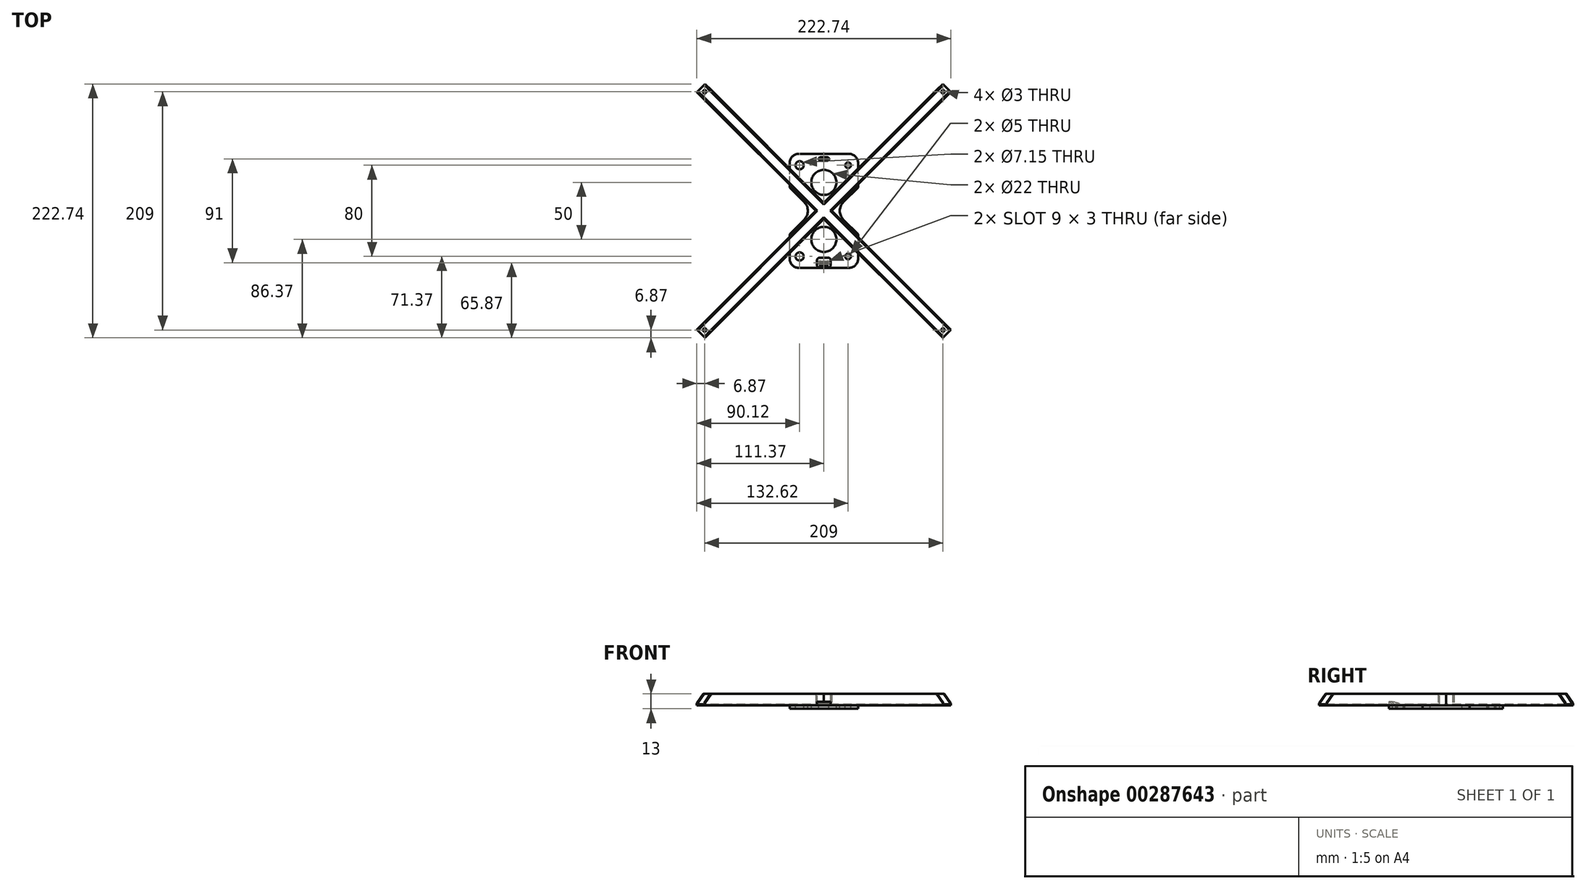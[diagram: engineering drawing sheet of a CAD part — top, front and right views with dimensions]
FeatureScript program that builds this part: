
annotation { "Feature Type Name" : "Feature", "Feature Type Description" : "" }
export const myFeature = defineFeature(function(context is Context, id is Id, definition is map)
    precondition{}
    {
        {
            var Q0;
            Q0=qCreatedBy(makeId("Top.planeOp"),FACE);
            var sketch = newSketch(context, id + "F0", { "sketchPlane" : qUnion([Q0])});
            skLineSegment(sketch, "E0.bottom", {"start": v(30, -50) * mm, "end": v(-30, -50) * mm});
            skLineSegment(sketch, "E0.top", {"start": v(30, 50) * mm, "end": v(-30, 50) * mm});
            skLineSegment(sketch, "E0.left", {"start": v(30, -50) * mm, "end": v(30, 50) * mm});
            skLineSegment(sketch, "E0.right", {"start": v(-30, -50) * mm, "end": v(-30, 50) * mm});
            skPoint(sketch, "E0.middle", {"position": v(0, 0) * mm});
            skSolve(sketch);
        }
        {
            var Q0;
            Q0 = qSketchRegion(id + "F0", true);
            extrude(context, id + "F1", {"entities" : qUnion([Q0]), "depth" : 3 * mm, "offsetDistance" : 25 * mm});
        }
        {
            var Q0;
            Q0=makeQuery(id+"F1.opExtrude","CAP_FACE",FACE,{"disambiguationData":[OSD([sQuery(id+"F0.wireOp",EDGE,"E0.bottom"),sQuery(id+"F0.wireOp",EDGE,"E0.top"),sQuery(id+"F0.wireOp",EDGE,"E0.left"),sQuery(id+"F0.wireOp",EDGE,"E0.right")])],"isStart":false});
            var sketch = newSketch(context, id + "F2", { "sketchPlane" : qUnion([Q0])});
            skCircle(sketch, "E1", {"center": v(0, 25) * mm, "radius": 11 * mm});
            skCircle(sketch, "E2", {"center": v(0, -25) * mm, "radius": 11 * mm});
            skCircle(sketch, "E3", {"center": v(25, 0) * mm, "radius": 11 * mm});
            skCircle(sketch, "E4", {"center": v(-25, 0) * mm, "radius": 11 * mm});
            skLineSegment(sketch, "E5", {"start": v(-3, 45.5) * mm, "end": v(3, 45.5) * mm});
            skLineSegment(sketch, "E6", {"start": v(-3, -45.5) * mm, "end": v(3, -45.5) * mm});
            skPoint(sketch, "E7", {"position": v(0, 45.5) * mm});
            skArc(sketch, "E8.0.startCap", {"start": v(-3, 44) * mm, "mid": v(-4.5, 45.5) * mm, "end": v(-3, 47) * mm});
            skArc(sketch, "E8.0.endCap", {"start": v(3, 47) * mm, "mid": v(4.5, 45.5) * mm, "end": v(3, 44) * mm});
            skLineSegment(sketch, "E8.0.left", {"start": v(-3, 47) * mm, "end": v(3, 47) * mm});
            skLineSegment(sketch, "E8.0.right", {"start": v(-3, 44) * mm, "end": v(3, 44) * mm});
            skArc(sketch, "E9.0.startCap", {"start": v(-3, -47) * mm, "mid": v(-4.5, -45.5) * mm, "end": v(-3, -44) * mm});
            skArc(sketch, "E9.0.endCap", {"start": v(3, -44) * mm, "mid": v(4.5, -45.5) * mm, "end": v(3, -47) * mm});
            skLineSegment(sketch, "E9.0.left", {"start": v(-3, -44) * mm, "end": v(3, -44) * mm});
            skLineSegment(sketch, "E9.0.right", {"start": v(-3, -47) * mm, "end": v(3, -47) * mm});
            skSolve(sketch);
        }
        {
            var Q0;
            Q0=makeQuery(id+"F2.imprint","IMPRINT",FACE,{"disambiguationData":[TD([[makeQuery(id+"F2.imprint","IMPRINT",EDGE,{"derivedFrom":sQuery(id+"F2.wireOp",EDGE,"E1")}),-1.0]])]});
            var sketch = newSketch(context, id + "F3", { "sketchPlane" : qUnion([Q0])});
            skLineSegment(sketch, "E10.bottom", {"start": v(21.25, 40) * mm, "end": v(-21.25, 40) * mm, "construction": true});
            skLineSegment(sketch, "E10.top", {"start": v(21.25, -40) * mm, "end": v(-21.25, -40) * mm, "construction": true});
            skLineSegment(sketch, "E10.left", {"start": v(21.25, 40) * mm, "end": v(21.25, -40) * mm, "construction": true});
            skLineSegment(sketch, "E10.right", {"start": v(-21.25, 40) * mm, "end": v(-21.25, -40) * mm, "construction": true});
            skPoint(sketch, "E10.middle", {"position": v(0, 0) * mm});
            skCircle(sketch, "E11", {"center": v(21.25, 40) * mm, "radius": 2.5 * mm});
            skCircle(sketch, "E12", {"center": v(21.25, -40) * mm, "radius": 2.5 * mm});
            skCircle(sketch, "E13", {"center": v(-21.25, -40) * mm, "radius": 3.58 * mm});
            skCircle(sketch, "E14", {"center": v(-21.25, 40) * mm, "radius": 3.57 * mm});
            skSolve(sketch);
        }
        {
            var Q0;
            Q0 = qSketchRegion(id + "F3", true);
            extrude(context, id + "F4", {"entities" : qUnion([Q0]), "operationType" : NewBodyOperationType.REMOVE, "endBound" : BoundingType.THROUGH_ALL, "oppositeDirection" : true, "depth" : 25 * mm, "offsetDistance" : 25 * mm});
        }
        {
            var Q0;
            Q0 = qSketchRegion(id + "F2", true);
            extrude(context, id + "F5", {"entities" : qUnion([Q0]), "operationType" : NewBodyOperationType.REMOVE, "endBound" : BoundingType.THROUGH_ALL, "oppositeDirection" : true, "depth" : 25 * mm, "offsetDistance" : 25 * mm});
        }
        {
            var Q0;
            Q0=makeQuery(id+"F1.opExtrude","CAP_FACE",FACE,{"disambiguationData":[OSD([sQuery(id+"F0.wireOp",EDGE,"E0.bottom"),sQuery(id+"F0.wireOp",EDGE,"E0.top"),sQuery(id+"F0.wireOp",EDGE,"E0.left"),sQuery(id+"F0.wireOp",EDGE,"E0.right")])],"isStart":false});
            var sketch = newSketch(context, id + "F6", { "sketchPlane" : qUnion([Q0])});
            skLineSegment(sketch, "E15", {"start": v(30, 20.56) * mm, "end": v(30, -20.56) * mm});
            skLineSegment(sketch, "E16", {"start": v(30, -20.56) * mm, "end": v(17.22, -7.78) * mm});
            skLineSegment(sketch, "E17", {"start": v(17.22, -7.78) * mm, "end": v(17.22, 7.78) * mm});
            skLineSegment(sketch, "E18", {"start": v(17.22, 7.78) * mm, "end": v(30, 20.56) * mm});
            skLineSegment(sketch, "E19", {"start": v(-30, 20.56) * mm, "end": v(-17.22, 7.78) * mm});
            skLineSegment(sketch, "E20", {"start": v(-17.22, 7.78) * mm, "end": v(-17.22, -7.78) * mm});
            skLineSegment(sketch, "E21", {"start": v(-17.22, -7.78) * mm, "end": v(-30, -20.56) * mm});
            skLineSegment(sketch, "E22", {"start": v(-30, -20.56) * mm, "end": v(-30, 20.56) * mm});
            skSolve(sketch);
        }
        {
            var Q0;
            Q0 = qSketchRegion(id + "F6", true);
            extrude(context, id + "F7", {"entities" : qUnion([Q0]), "operationType" : NewBodyOperationType.REMOVE, "endBound" : BoundingType.THROUGH_ALL, "oppositeDirection" : true, "depth" : 25 * mm, "offsetDistance" : 25 * mm});
        }
        {
            var Q0;
            Q0=makeQuery(id+"F1.opExtrude","SWEPT_EDGE",EDGE,{"disambiguationData":[OSD([sQuery(id+"F0.wireOp",EDGE,"E0.bottom"),sQuery(id+"F0.wireOp",EDGE,"E0.left")])]});
            var Q1;
            Q1=makeQuery(id+"F1.opExtrude","SWEPT_EDGE",EDGE,{"disambiguationData":[OSD([sQuery(id+"F0.wireOp",EDGE,"E0.bottom"),sQuery(id+"F0.wireOp",EDGE,"E0.right")])]});
            var Q2;
            Q2=makeQuery(id+"F1.opExtrude","SWEPT_EDGE",EDGE,{"disambiguationData":[OSD([sQuery(id+"F0.wireOp",EDGE,"E0.top"),sQuery(id+"F0.wireOp",EDGE,"E0.left")])]});
            var Q3;
            Q3=makeQuery(id+"F1.opExtrude","SWEPT_EDGE",EDGE,{"disambiguationData":[OSD([sQuery(id+"F0.wireOp",EDGE,"E0.top"),sQuery(id+"F0.wireOp",EDGE,"E0.right")])]});
            fillet(context, id + "F8", {"entities" : qUnion([Q0, Q1, Q2, Q3]), "radius" : 8 * mm, "tangentPropagation" : true, "allowEdgeOverflow" : false});
        }
        {
            var Q0;
            Q0=makeQuery(id+"F1.opExtrude","CAP_FACE",FACE,{"disambiguationData":[OSD([sQuery(id+"F0.wireOp",EDGE,"E0.bottom"),sQuery(id+"F0.wireOp",EDGE,"E0.top"),sQuery(id+"F0.wireOp",EDGE,"E0.left"),sQuery(id+"F0.wireOp",EDGE,"E0.right")])],"isStart":false});
            var sketch = newSketch(context, id + "F9", { "sketchPlane" : qUnion([Q0])});
            skLineSegment(sketch, "E23", {"start": v(-107.83, 107.83) * mm, "end": v(107.83, -107.83) * mm, "construction": true});
            skLineSegment(sketch, "E24", {"start": v(-104.3, 111.37) * mm, "end": v(-111.37, 104.3) * mm});
            skLineSegment(sketch, "E25", {"start": v(-111.37, 104.3) * mm, "end": v(104.3, -111.37) * mm});
            skLineSegment(sketch, "E26", {"start": v(104.3, -111.37) * mm, "end": v(111.37, -104.3) * mm});
            skLineSegment(sketch, "E27", {"start": v(111.37, -104.3) * mm, "end": v(-104.3, 111.37) * mm});
            skSolve(sketch);
        }
        {
            var Q0;
            Q0 = qSketchRegion(id + "F9", true);
            extrude(context, id + "F10", {"entities" : qUnion([Q0]), "depth" : 10 * mm, "offsetDistance" : 25 * mm});
        }
        {
            var Q0;
            Q0=makeQuery(id+"F10.opExtrude","CAP_FACE",FACE,{"disambiguationData":[OSD([sQuery(id+"F9.wireOp",EDGE,"E24"),sQuery(id+"F9.wireOp",EDGE,"E25"),sQuery(id+"F9.wireOp",EDGE,"E26"),sQuery(id+"F9.wireOp",EDGE,"E27")])],"isStart":false});
            var sketch = newSketch(context, id + "F11", { "sketchPlane" : qUnion([Q0])});
            skLineSegment(sketch, "E28", {"start": v(-105, 110.66) * mm, "end": v(-110.66, 105) * mm});
            skLineSegment(sketch, "E29", {"start": v(-110.66, 105) * mm, "end": v(105, -110.66) * mm});
            skLineSegment(sketch, "E30", {"start": v(105, -110.66) * mm, "end": v(110.66, -105) * mm});
            skLineSegment(sketch, "E31", {"start": v(110.66, -105) * mm, "end": v(-105, 110.66) * mm});
            skSolve(sketch);
        }
        {
            var Q0;
            Q0 = qSketchRegion(id + "F11", true);
            extrude(context, id + "F12", {"entities" : qUnion([Q0]), "operationType" : NewBodyOperationType.REMOVE, "oppositeDirection" : true, "depth" : 9 * mm, "offsetDistance" : 25 * mm});
        }
        {
            var Q0;
            Q0=makeQuery(id+"F10.opExtrude","SWEPT_FACE",FACE,{"disambiguationData":[OSD([sQuery(id+"F9.wireOp",EDGE,"E27")])]});
            var sketch = newSketch(context, id + "F13", { "sketchPlane" : qUnion([Q0])});
            skLineSegment(sketch, "E32.bottom", {"start": v(5, 13) * mm, "end": v(-5, 13) * mm});
            skLineSegment(sketch, "E32.top", {"start": v(5, 3) * mm, "end": v(-5, 3) * mm});
            skLineSegment(sketch, "E32.left", {"start": v(5, 13) * mm, "end": v(5, 3) * mm});
            skLineSegment(sketch, "E32.right", {"start": v(-5, 13) * mm, "end": v(-5, 3) * mm});
            skSolve(sketch);
        }
        {
            var Q0;
            Q0 = qSketchRegion(id + "F13", true);
            extrude(context, id + "F14", {"entities" : qUnion([Q0]), "depth" : (305 / 2 - 5) * mm, "offsetDistance" : 25 * mm});
        }
        {
            var Q0;
            Q0=makeQuery(id+"F14.opExtrude","CAP_FACE",FACE,{"disambiguationData":[OSD([sQuery(id+"F13.wireOp",EDGE,"E32.bottom"),sQuery(id+"F13.wireOp",EDGE,"E32.top"),sQuery(id+"F13.wireOp",EDGE,"E32.left"),sQuery(id+"F13.wireOp",EDGE,"E32.right")])],"isStart":false});
            var sketch = newSketch(context, id + "F15", { "sketchPlane" : qUnion([Q0])});
            skLineSegment(sketch, "E33.bottom", {"start": v(4, 13) * mm, "end": v(-4, 13) * mm});
            skLineSegment(sketch, "E33.top", {"start": v(4, 4) * mm, "end": v(-4, 4) * mm});
            skLineSegment(sketch, "E33.left", {"start": v(4, 13) * mm, "end": v(4, 4) * mm});
            skLineSegment(sketch, "E33.right", {"start": v(-4, 13) * mm, "end": v(-4, 4) * mm});
            skSolve(sketch);
        }
        {
            var Q0;
            Q0 = qSketchRegion(id + "F15", true);
            extrude(context, id + "F16", {"entities" : qUnion([Q0]), "operationType" : NewBodyOperationType.REMOVE, "endBound" : BoundingType.THROUGH_ALL, "oppositeDirection" : true, "depth" : 25 * mm, "offsetDistance" : 25 * mm});
        }
        {
            var Q0;
            Q0=qCreatedBy(makeId("Front.planeOp"),FACE);
            var Q1;
            Q1=qCreatedBy(makeId("Right.planeOp"),FACE);
            cPlane(context, id + "F17", {"entities" : qUnion([Q0, Q1]), "cplaneType" : CPlaneType.MID_PLANE, "offset" : 25 * mm, "width" : 150 * mm, "height" : 150 * mm});
        }
        {
            var Q0;
            Q0=makeQuery(id+"F14.opExtrude","SWEPT_BODY",BODY,{"disambiguationData":[OSD([sQuery(id+"F13.wireOp",EDGE,"E32.bottom"),sQuery(id+"F13.wireOp",EDGE,"E32.top"),sQuery(id+"F13.wireOp",EDGE,"E32.left"),sQuery(id+"F13.wireOp",EDGE,"E32.right")])]});
            var Q1;
            Q1=qCreatedBy(id+"F17.planeOp",FACE);
            mirror(context, id + "F18", {"entities" : qUnion([Q0]), "mirrorPlane" : qUnion([Q1])});
        }
        {
            var Q0;
            {var subQ0=sQuery(id+"F13.wireOp",EDGE,"E32.bottom");var subQ1=sQuery(id+"F13.wireOp",EDGE,"E32.left");Q0=makeQuery(id+"F16.boolean.opBoolean","SPLIT",EDGE,{"disambiguationData":[TD([makeQuery(id+"F14.opExtrude","SWEPT_FACE",FACE,{"disambiguationData":[OSD([subQ1])]})])],"derivedFrom":makeQuery(id+"F14.opExtrude","CAP_EDGE",EDGE,{"disambiguationData":[OSD([subQ0])],"isStart":false})});}
            var Q1;
            {var subQ0=sQuery(id+"F13.wireOp",EDGE,"E32.bottom");var subQ1=sQuery(id+"F13.wireOp",EDGE,"E32.right");Q1=makeQuery(id+"F16.boolean.opBoolean","SPLIT",EDGE,{"disambiguationData":[TD([makeQuery(id+"F14.opExtrude","SWEPT_FACE",FACE,{"disambiguationData":[OSD([subQ1])]})])],"derivedFrom":makeQuery(id+"F14.opExtrude","CAP_EDGE",EDGE,{"disambiguationData":[OSD([subQ0])],"isStart":false})});}
            var Q2;
            {var subQ0=sQuery(id+"F9.wireOp",EDGE,"E26");var subQ1=sQuery(id+"F9.wireOp",EDGE,"E25");Q2=makeQuery(id+"F12.boolean.opBoolean","SPLIT",EDGE,{"disambiguationData":[TD([makeQuery(id+"F10.opExtrude","SWEPT_FACE",FACE,{"disambiguationData":[OSD([subQ1])]})])],"derivedFrom":makeQuery(id+"F10.opExtrude","CAP_EDGE",EDGE,{"disambiguationData":[OSD([subQ0])],"isStart":false})});}
            var Q3;
            {var subQ0=sQuery(id+"F9.wireOp",EDGE,"E27");var subQ1=sQuery(id+"F9.wireOp",EDGE,"E26");Q3=makeQuery(id+"F12.boolean.opBoolean","SPLIT",EDGE,{"disambiguationData":[TD([makeQuery(id+"F10.opExtrude","SWEPT_FACE",FACE,{"disambiguationData":[OSD([subQ0])]})])],"derivedFrom":makeQuery(id+"F10.opExtrude","CAP_EDGE",EDGE,{"disambiguationData":[OSD([subQ1])],"isStart":false})});}
            var Q4;
            {var subQ0=sQuery(id+"F13.wireOp",EDGE,"E32.bottom");var subQ1=sQuery(id+"F13.wireOp",EDGE,"E32.right");Q4=makeQuery(id+"F18.opPattern","COPY",EDGE,{"derivedFrom":makeQuery(id+"F16.boolean.opBoolean","SPLIT",EDGE,{"disambiguationData":[TD([makeQuery(id+"F14.opExtrude","SWEPT_FACE",FACE,{"disambiguationData":[OSD([subQ1])]})])],"derivedFrom":makeQuery(id+"F14.opExtrude","CAP_EDGE",EDGE,{"disambiguationData":[OSD([subQ0])],"isStart":false})}),"instanceName":"1"});}
            var Q5;
            {var subQ0=sQuery(id+"F13.wireOp",EDGE,"E32.bottom");var subQ1=sQuery(id+"F13.wireOp",EDGE,"E32.left");Q5=makeQuery(id+"F18.opPattern","COPY",EDGE,{"derivedFrom":makeQuery(id+"F16.boolean.opBoolean","SPLIT",EDGE,{"disambiguationData":[TD([makeQuery(id+"F14.opExtrude","SWEPT_FACE",FACE,{"disambiguationData":[OSD([subQ1])]})])],"derivedFrom":makeQuery(id+"F14.opExtrude","CAP_EDGE",EDGE,{"disambiguationData":[OSD([subQ0])],"isStart":false})}),"instanceName":"1"});}
            var Q6;
            {var subQ0=sQuery(id+"F9.wireOp",EDGE,"E24");var subQ1=sQuery(id+"F9.wireOp",EDGE,"E27");Q6=makeQuery(id+"F12.boolean.opBoolean","SPLIT",EDGE,{"disambiguationData":[TD([makeQuery(id+"F10.opExtrude","SWEPT_FACE",FACE,{"disambiguationData":[OSD([subQ1])]})])],"derivedFrom":makeQuery(id+"F10.opExtrude","CAP_EDGE",EDGE,{"disambiguationData":[OSD([subQ0])],"isStart":false})});}
            var Q7;
            {var subQ0=sQuery(id+"F9.wireOp",EDGE,"E24");var subQ1=sQuery(id+"F9.wireOp",EDGE,"E25");Q7=makeQuery(id+"F12.boolean.opBoolean","SPLIT",EDGE,{"disambiguationData":[TD([makeQuery(id+"F10.opExtrude","SWEPT_FACE",FACE,{"disambiguationData":[OSD([subQ1])]})])],"derivedFrom":makeQuery(id+"F10.opExtrude","CAP_EDGE",EDGE,{"disambiguationData":[OSD([subQ0])],"isStart":false})});}
            chamfer(context, id + "F19", {"entities" : qUnion([Q0, Q1, Q2, Q3, Q4, Q5, Q6, Q7]), "width" : 8 * mm, "tangentPropagation" : true});
        }
        {
            var Q0;
            Q0=makeQuery(id+"F12.boolean.opBoolean","COPY",FACE,{"derivedFrom":makeQuery(id+"F12.opExtrude","CAP_FACE",FACE,{"disambiguationData":[OSD([sQuery(id+"F11.wireOp",EDGE,"E28"),sQuery(id+"F11.wireOp",EDGE,"E29"),sQuery(id+"F11.wireOp",EDGE,"E30"),sQuery(id+"F11.wireOp",EDGE,"E31")])],"isStart":false})});
            var sketch = newSketch(context, id + "F20", { "sketchPlane" : qUnion([Q0])});
            skLineSegment(sketch, "E34.bottom", {"start": v(-104.5, -104.5) * mm, "end": v(104.5, -104.5) * mm, "construction": true});
            skLineSegment(sketch, "E34.top", {"start": v(-104.5, 104.5) * mm, "end": v(104.5, 104.5) * mm, "construction": true});
            skLineSegment(sketch, "E34.left", {"start": v(-104.5, -104.5) * mm, "end": v(-104.5, 104.5) * mm, "construction": true});
            skLineSegment(sketch, "E34.right", {"start": v(104.5, -104.5) * mm, "end": v(104.5, 104.5) * mm, "construction": true});
            skPoint(sketch, "E34.middle", {"position": v(0, 0) * mm});
            skCircle(sketch, "E35", {"center": v(-104.5, -104.5) * mm, "radius": 1.5 * mm});
            skCircle(sketch, "E36", {"center": v(104.5, -104.5) * mm, "radius": 1.5 * mm});
            skCircle(sketch, "E37", {"center": v(104.5, 104.5) * mm, "radius": 1.5 * mm});
            skCircle(sketch, "E38", {"center": v(-104.5, 104.5) * mm, "radius": 1.5 * mm});
            skSolve(sketch);
        }
        {
            var Q0;
            Q0 = qSketchRegion(id + "F20", true);
            extrude(context, id + "F21", {"entities" : qUnion([Q0]), "operationType" : NewBodyOperationType.REMOVE, "endBound" : BoundingType.THROUGH_ALL, "oppositeDirection" : true, "depth" : 25 * mm, "offsetDistance" : 25 * mm});
        }
        {
            var Q0;
            Q0=makeQuery(id+"F1.opExtrude","SWEPT_BODY",BODY,{"disambiguationData":[OSD([sQuery(id+"F0.wireOp",EDGE,"E0.bottom"),sQuery(id+"F0.wireOp",EDGE,"E0.top"),sQuery(id+"F0.wireOp",EDGE,"E0.left"),sQuery(id+"F0.wireOp",EDGE,"E0.right")])]});
            var Q1;
            Q1=makeQuery(id+"F10.opExtrude","SWEPT_BODY",BODY,{"disambiguationData":[OSD([sQuery(id+"F9.wireOp",EDGE,"E24"),sQuery(id+"F9.wireOp",EDGE,"E25"),sQuery(id+"F9.wireOp",EDGE,"E26"),sQuery(id+"F9.wireOp",EDGE,"E27")])]});
            var Q2;
            Q2=makeQuery(id+"F14.opExtrude","SWEPT_BODY",BODY,{"disambiguationData":[OSD([sQuery(id+"F13.wireOp",EDGE,"E32.bottom"),sQuery(id+"F13.wireOp",EDGE,"E32.top"),sQuery(id+"F13.wireOp",EDGE,"E32.left"),sQuery(id+"F13.wireOp",EDGE,"E32.right")])]});
            var Q3;
            Q3=makeQuery(id+"F18.opPattern","COPY",BODY,{"derivedFrom":makeQuery(id+"F14.opExtrude","SWEPT_BODY",BODY,{"disambiguationData":[OSD([sQuery(id+"F13.wireOp",EDGE,"E32.bottom"),sQuery(id+"F13.wireOp",EDGE,"E32.top"),sQuery(id+"F13.wireOp",EDGE,"E32.left"),sQuery(id+"F13.wireOp",EDGE,"E32.right")])]}),"instanceName":"1"});
            booleanBodies(context, id + "F22", {"operationType" : BooleanOperationType.UNION, "tools" : qUnion([Q0, Q1, Q2, Q3])});
        }
        {
            var Q0;
            {var subQ1=sQuery(id+"F0.wireOp",EDGE,"E0.left");var subQ2=sQuery(id+"F0.wireOp",EDGE,"E0.bottom");var subQ3=sQuery(id+"F0.wireOp",EDGE,"E0.right");Q0=makeQuery(id+"F22.opBoolean","SPLIT",FACE,{"disambiguationData":[TD([makeQuery(id+"F1.opExtrude","SWEPT_FACE",FACE,{"disambiguationData":[OSD([subQ2])]})])],"derivedFrom":makeQuery(id+"F1.opExtrude","CAP_FACE",FACE,{"disambiguationData":[OSD([subQ2,sQuery(id+"F0.wireOp",EDGE,"E0.top"),subQ1,subQ3])],"isStart":false})});}
            var sketch = newSketch(context, id + "F23", { "sketchPlane" : qUnion([Q0])});
            skLineSegment(sketch, "E39.bottom", {"start": v(-6, -50) * mm, "end": v(6, -50) * mm});
            skLineSegment(sketch, "E39.top", {"start": v(-6, -41) * mm, "end": v(6, -41) * mm});
            skLineSegment(sketch, "E39.left", {"start": v(-6, -50) * mm, "end": v(-6, -41) * mm});
            skLineSegment(sketch, "E39.right", {"start": v(6, -50) * mm, "end": v(6, -41) * mm});
            skPoint(sketch, "E39.middle", {"position": v(0, -45.5) * mm});
            skPoint(sketch, "E39.middle.positionSnap0", {"position": v(0, -47) * mm});
            skPoint(sketch, "E39.centerSnap0", {"position": v(0, -47) * mm});
            skLineSegment(sketch, "E40.bottom", {"start": v(3.2, -46.95) * mm, "end": v(-3.2, -46.95) * mm});
            skLineSegment(sketch, "E40.top", {"start": v(3.2, -47.05) * mm, "end": v(-3.2, -47.05) * mm});
            skLineSegment(sketch, "E40.left", {"start": v(3.2, -46.95) * mm, "end": v(3.2, -47.05) * mm});
            skLineSegment(sketch, "E40.right", {"start": v(-3.2, -46.95) * mm, "end": v(-3.2, -47.05) * mm});
            skSolve(sketch);
        }
        {
            var Q0;
            Q0 = qSketchRegion(id + "F23", true);
            extrude(context, id + "F24", {"entities" : qUnion([Q0]), "depth" : 3 * mm, "offsetDistance" : 25 * mm});
        }
        {
            var Q0;
            Q0=makeQuery(id+"F24.opExtrude","CAP_EDGE",EDGE,{"disambiguationData":[OSD([sQuery(id+"F23.wireOp",EDGE,"E40.top")])],"isStart":false});
            var Q1;
            Q1=makeQuery(id+"F24.opExtrude","CAP_EDGE",EDGE,{"disambiguationData":[OSD([sQuery(id+"F23.wireOp",EDGE,"E40.bottom")])],"isStart":true});
            chamfer(context, id + "F25", {"entities" : qUnion([Q0, Q1]), "width" : 2.5 * mm, "tangentPropagation" : true});
        }
        {
            var Q0;
            Q0=makeQuery(id+"F24.opExtrude","SWEPT_EDGE",EDGE,{"disambiguationData":[OSD([sQuery(id+"F0.wireOp",EDGE,"E0.bottom"),sQuery(id+"F23.wireOp",EDGE,"E39.bottom"),sQuery(id+"F23.wireOp",EDGE,"E39.left")])]});
            var Q1;
            Q1=makeQuery(id+"F24.opExtrude","SWEPT_EDGE",EDGE,{"disambiguationData":[OSD([sQuery(id+"F23.wireOp",EDGE,"E39.top"),sQuery(id+"F23.wireOp",EDGE,"E39.left")])]});
            var Q2;
            Q2=makeQuery(id+"F24.opExtrude","SWEPT_EDGE",EDGE,{"disambiguationData":[OSD([sQuery(id+"F0.wireOp",EDGE,"E0.bottom"),sQuery(id+"F23.wireOp",EDGE,"E39.bottom"),sQuery(id+"F23.wireOp",EDGE,"E39.right")])]});
            var Q3;
            Q3=makeQuery(id+"F24.opExtrude","SWEPT_EDGE",EDGE,{"disambiguationData":[OSD([sQuery(id+"F23.wireOp",EDGE,"E39.top"),sQuery(id+"F23.wireOp",EDGE,"E39.right")])]});
            fillet(context, id + "F26", {"entities" : qUnion([Q0, Q1, Q2, Q3]), "radius" : 2.5 * mm, "tangentPropagation" : true, "allowEdgeOverflow" : false});
        }
        {
            var Q0;
            Q0=makeQuery(id+"F24.opExtrude","CAP_EDGE",EDGE,{"disambiguationData":[OSD([sQuery(id+"F23.wireOp",EDGE,"E39.top")])],"isStart":false});
            chamfer(context, id + "F27", {"entities" : qUnion([Q0]), "chamferType" : ChamferType.TWO_OFFSETS, "width1" : 1.5 * mm, "oppositeDirection" : false, "width2" : 5 * mm});
        }
    });
